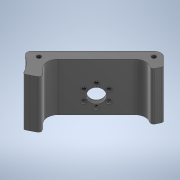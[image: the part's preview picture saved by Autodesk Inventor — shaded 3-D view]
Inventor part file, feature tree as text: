
AUTODESK INVENTOR PART (.ipt)
format: ipt  version: 2020 (Build 240168000, 168)  size: 576,000 bytes
history: native  units: mm
features: extrude x4, sketch x3, other x1, chamfer x1, fillet x1
ambient origin geometry x8: Origin, YZ Plane, XZ Plane, XY Plane, X Axis, Y Axis, Z Axis, Center Point
bodies: Body1 (feature_tree)
feature tree (10):
  other  "Твердое тело1"
  sketch  "Эскиз1"
  extrude  "Выдавливание10"  Depth=3.0mm
  sketch  "Эскиз6"
  extrude  "Выдавливание13"  Depth=6.0mm
  extrude  "Выдавливание14"  Depth=35.0mm TaperAngle=0.0deg
  chamfer  "Фаска3"  Distance=59.0mm
  extrude  "Выдавливание15"  Depth=21.3mm
  fillet  "Сопряжение1"  Radius=15.0mm
  sketch  "Эскиз7"
